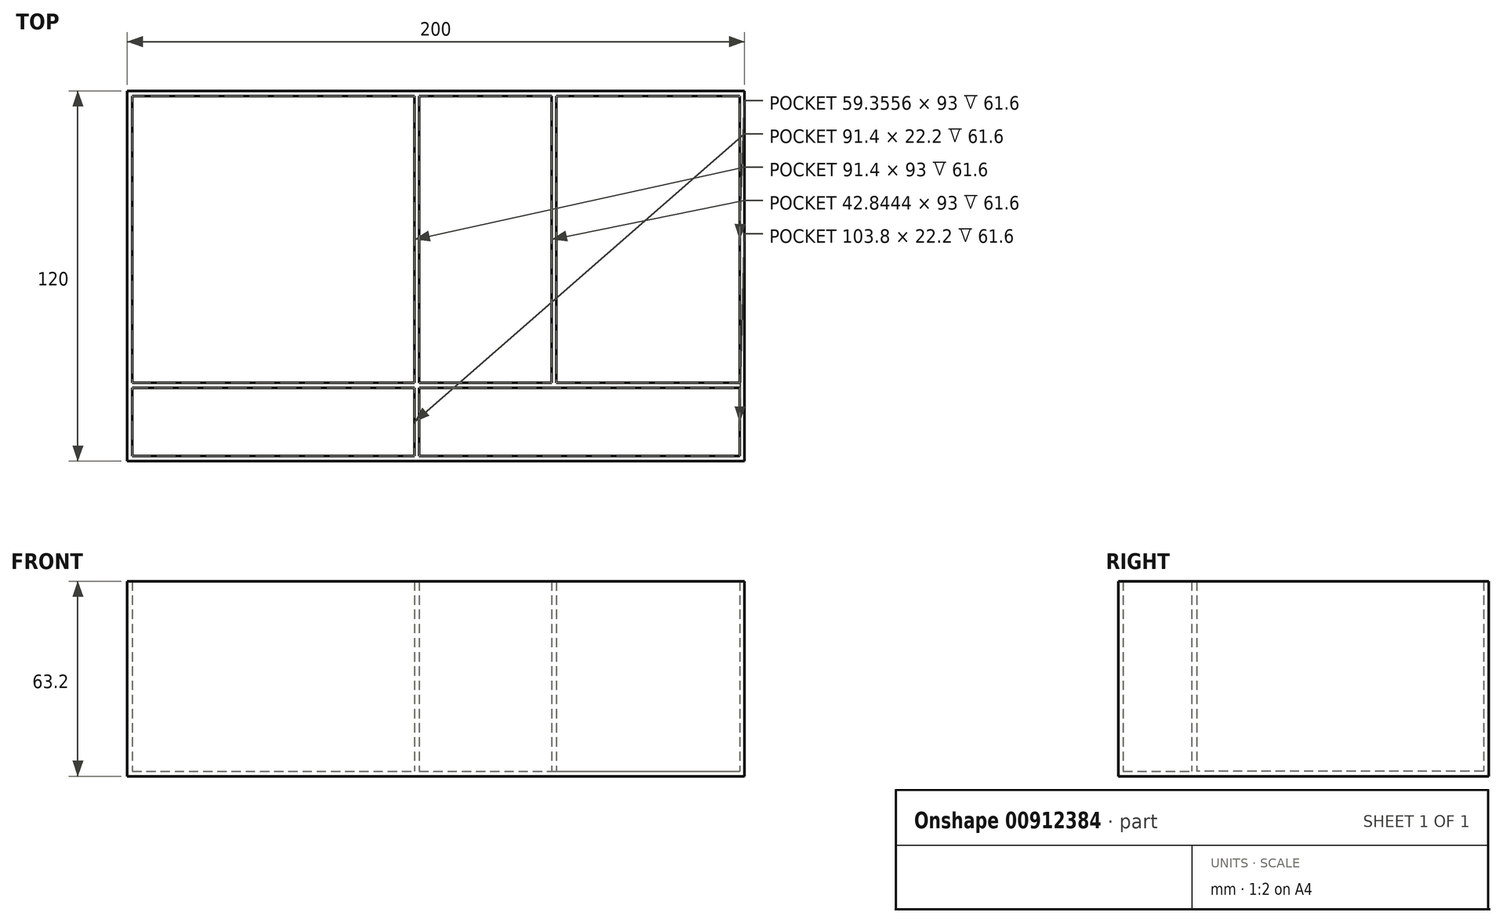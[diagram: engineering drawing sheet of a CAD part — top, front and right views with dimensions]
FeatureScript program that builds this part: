
annotation { "Feature Type Name" : "Feature", "Feature Type Description" : "" }
export const myFeature = defineFeature(function(context is Context, id is Id, definition is map)
    precondition{}
    {
        {
            assignVariable(context, id + "F0", {"name" : "wall", "anyValue" : 1.6});
        }
        {
            assignVariable(context, id + "F1", {"name" : "k_x", "anyValue" : 60});
        }
        {
            var Q0;
            Q0=qCreatedBy(makeId("Top.planeOp"),FACE);
            var sketch = newSketch(context, id + "F2", { "sketchPlane" : qUnion([Q0])});
            skLineSegment(sketch, "E0.bottom", {"start": v(-25.9, 98.49) * mm, "end": v(174.1, 98.49) * mm});
            skLineSegment(sketch, "E0.top", {"start": v(-25.9, -21.51) * mm, "end": v(174.1, -21.51) * mm});
            skLineSegment(sketch, "E0.left", {"start": v(-25.9, 98.49) * mm, "end": v(-25.9, -21.51) * mm});
            skLineSegment(sketch, "E0.right", {"start": v(174.1, 98.49) * mm, "end": v(174.1, -21.51) * mm});
            skSolve(sketch);
        }
        {
            var Q0;
            Q0=makeQuery(id+"F2.imprint","IMPRINT",FACE,{"disambiguationData":[TD([[makeQuery(id+"F2.imprint","IMPRINT",EDGE,{"derivedFrom":sQuery(id+"F2.wireOp",EDGE,"E0.bottom")}),-1.0]])]});
            extrude(context, id + "F3", {"entities" : qUnion([Q0]), "depth" : ((getVariable(context, 'wall') * 2) + getVariable(context, 'k_x')) * mm, "offsetDistance" : 25 * mm});
        }
        {
            var Q0;
            Q0=makeQuery(id+"F3.opExtrude","CAP_FACE",FACE,{"disambiguationData":[OSD([sQuery(id+"F2.wireOp",EDGE,"E0.bottom"),sQuery(id+"F2.wireOp",EDGE,"E0.top"),sQuery(id+"F2.wireOp",EDGE,"E0.left"),sQuery(id+"F2.wireOp",EDGE,"E0.right")])],"isStart":false});
            shell(context, id + "F4", {"entities" : qUnion([Q0]), "thickness" : getVariable(context, 'wall') * mm});
        }
        {
            var Q0;
            Q0=makeQuery(id+"F4.opShell","OFFSET_FACE",FACE,{"disambiguationData":[OSD([sQuery(id+"F2.wireOp",EDGE,"E0.bottom"),sQuery(id+"F2.wireOp",EDGE,"E0.top"),sQuery(id+"F2.wireOp",EDGE,"E0.left"),sQuery(id+"F2.wireOp",EDGE,"E0.right")])]});
            var sketch = newSketch(context, id + "F5", { "sketchPlane" : qUnion([Q0])});
            skLineSegment(sketch, "E1", {"start": v(-24.3, 3.89) * mm, "end": v(172.5, 3.89) * mm});
            skLineSegment(sketch, "E2", {"start": v(-24.3, 2.29) * mm, "end": v(172.5, 2.29) * mm});
            skLineSegment(sketch, "E3", {"start": v(68.7, -19.91) * mm, "end": v(68.7, 96.89) * mm});
            skLineSegment(sketch, "E4", {"start": v(67.1, -19.91) * mm, "end": v(67.1, 96.89) * mm});
            skLineSegment(sketch, "E5", {"start": v(111.55, 3.89) * mm, "end": v(111.55, 96.89) * mm});
            skLineSegment(sketch, "E6", {"start": v(113.15, 3.89) * mm, "end": v(113.15, 96.89) * mm});
            skSolve(sketch);
        }
        {
            var Q0;
            Q0 = qSketchRegion(id + "F5", true);
            var Q1;
            {var subQ0=sQuery(id+"F5.wireOp",EDGE,"E4");var subQ1=sQuery(id+"F5.wireOp",EDGE,"E2");var subQ2=makeQuery(id+"F5.imprint","INTERSECT",VERTEX,{"derivedFrom":[subQ1,subQ0]});Q1=makeQuery(id+"F5.imprint","IMPRINT",FACE,{"disambiguationData":[TD([[makeQuery(id+"F5.imprint","IMPRINT",EDGE,{"disambiguationData":[TD([[subQ2,-1.0]])],"derivedFrom":subQ1}),-1.0]])]});}
            var Q2;
            {var subQ0=sQuery(id+"F5.wireOp",EDGE,"E1");var subQ5=makeQuery(id+"F5.imprint","INTERSECT",VERTEX,{"derivedFrom":[subQ0,sQuery(id+"F5.wireOp",EDGE,"E5")]});Q2=makeQuery(id+"F5.imprint","IMPRINT",FACE,{"disambiguationData":[TD([[makeQuery(id+"F5.imprint","IMPRINT",EDGE,{"disambiguationData":[TD([[subQ5,1.0]])],"derivedFrom":subQ0}),-1.0]])]});}
            var Q3;
            {var subQ0=sQuery(id+"F5.wireOp",EDGE,"E4");var subQ1=sQuery(id+"F5.wireOp",EDGE,"E1");var subQ2=makeQuery(id+"F5.imprint","INTERSECT",VERTEX,{"derivedFrom":[subQ1,subQ0]});Q3=makeQuery(id+"F5.imprint","IMPRINT",FACE,{"disambiguationData":[TD([[makeQuery(id+"F5.imprint","IMPRINT",EDGE,{"disambiguationData":[TD([[subQ2,-1.0]])],"derivedFrom":subQ1}),1.0]])]});}
            var Q4;
            {var subQ0=sQuery(id+"F5.wireOp",EDGE,"E1");var subQ4=sQuery(id+"F5.wireOp",EDGE,"E4");var subQ5=makeQuery(id+"F5.imprint","INTERSECT",VERTEX,{"derivedFrom":[subQ0,subQ4]});Q4=makeQuery(id+"F5.imprint","IMPRINT",FACE,{"disambiguationData":[TD([[makeQuery(id+"F5.imprint","IMPRINT",EDGE,{"disambiguationData":[TD([[subQ5,1.0]])],"derivedFrom":subQ4}),1.0]])]});}
            var Q5;
            {var subQ0=sQuery(id+"F5.wireOp",EDGE,"E5");Q5=makeQuery(id+"F5.imprint","IMPRINT",FACE,{"disambiguationData":[TD([[makeQuery(id+"F5.imprint","IMPRINT",EDGE,{"derivedFrom":subQ0}),-1.0]])]});}
            var Q6;
            Q6=makeQuery(id+"F3.opExtrude","CAP_FACE",FACE,{"disambiguationData":[OSD([sQuery(id+"F2.wireOp",EDGE,"E0.bottom"),sQuery(id+"F2.wireOp",EDGE,"E0.top"),sQuery(id+"F2.wireOp",EDGE,"E0.left"),sQuery(id+"F2.wireOp",EDGE,"E0.right")])],"isStart":false});
            extrude(context, id + "F6", {"entities" : qUnion([Q0, Q1, Q2, Q3, Q4, Q5]), "operationType" : NewBodyOperationType.ADD, "endBound" : BoundingType.UP_TO_SURFACE, "depth" : 25 * mm, "endBoundEntityFace" : qUnion([Q6]), "offsetDistance" : 25 * mm});
        }
    });
